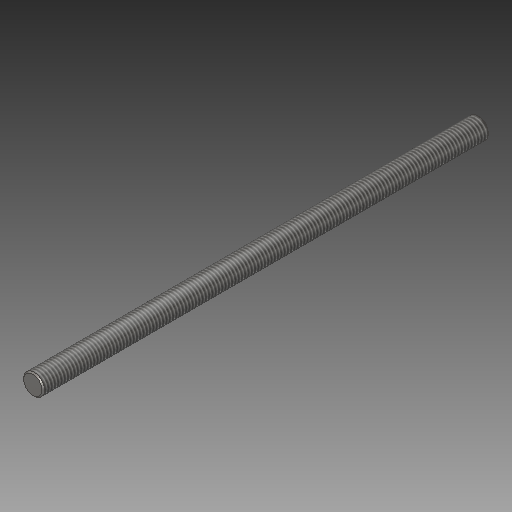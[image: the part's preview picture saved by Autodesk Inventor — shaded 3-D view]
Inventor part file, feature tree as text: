
AUTODESK INVENTOR PART (.ipt)
format: ipt  version: 2019 (Build 230136000, 136)  size: 115,200 bytes
history: native  units: mm
features: extrude x1, chamfer x1, thread x1, sketch x1
ambient origin geometry x8: Origin, YZ Plane, XZ Plane, XY Plane, X Axis, Y Axis, Z Axis, Center Point
bodies: Solid1 (feature_tree)
feature tree (4):
  extrude  "Extrusion1"  Depth=170.0mm TaperAngle=0.0deg
  chamfer  "Chamfer1"  Distance=0.5mm Angle=45.0deg
  thread  "Thread1"  [1 undecoded]
  sketch  "Sketch1"  dims[d0=8.0mm d1=170.0mm d2=0.0mm d3=0.5mm d4=2.0mm d5=45.0deg d6=10.0mm d7=0.0mm]
note: 1 required parameter value undecoded (feature->parameter linkage not recoverable at this tier; creation-order binding heuristic only, values carry confidence <= 0.55)
